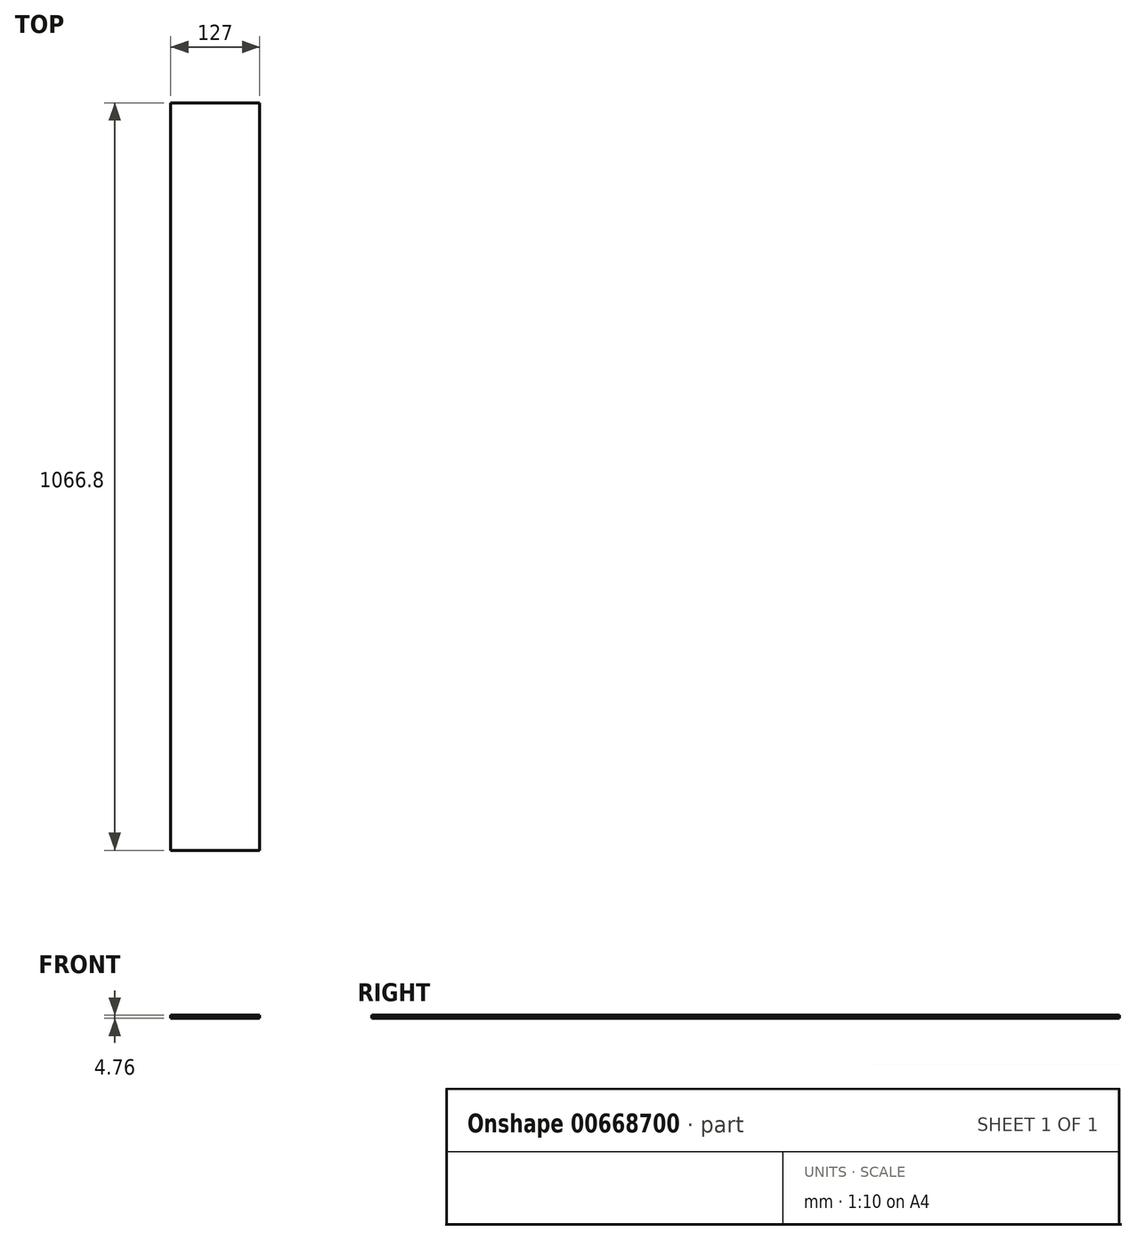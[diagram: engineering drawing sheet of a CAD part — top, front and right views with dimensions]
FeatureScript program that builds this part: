
annotation { "Feature Type Name" : "Feature", "Feature Type Description" : "" }
export const myFeature = defineFeature(function(context is Context, id is Id, definition is map)
    precondition{}
    {
        {
            var Q0;
            Q0=qCreatedBy(makeId("Top.planeOp"),FACE);
            var sketch = newSketch(context, id + "F0", { "sketchPlane" : qUnion([Q0])});
            skLineSegment(sketch, "E0.bottom", {"start": v(63.5, 533.4) * mm, "end": v(-63.5, 533.4) * mm});
            skLineSegment(sketch, "E0.top", {"start": v(63.5, -533.4) * mm, "end": v(-63.5, -533.4) * mm});
            skLineSegment(sketch, "E0.left", {"start": v(63.5, -381) * mm, "end": v(63.5, -533.4) * mm});
            skLineSegment(sketch, "E0.right", {"start": v(-63.5, 533.4) * mm, "end": v(-63.5, -533.4) * mm});
            skPoint(sketch, "E0.middle", {"position": v(0, 0) * mm});
            skLineSegment(sketch, "E1", {"start": v(63.5, 533.4) * mm, "end": v(63.5, -381) * mm});
            skSolve(sketch);
        }
        {
            var Q0;
            Q0=qSketchRegion(id+"F0",true);
            extrude(context, id + "F1", {"entities" : qUnion([Q0]), "depth" : 4.76 * mm});
        }
    });
